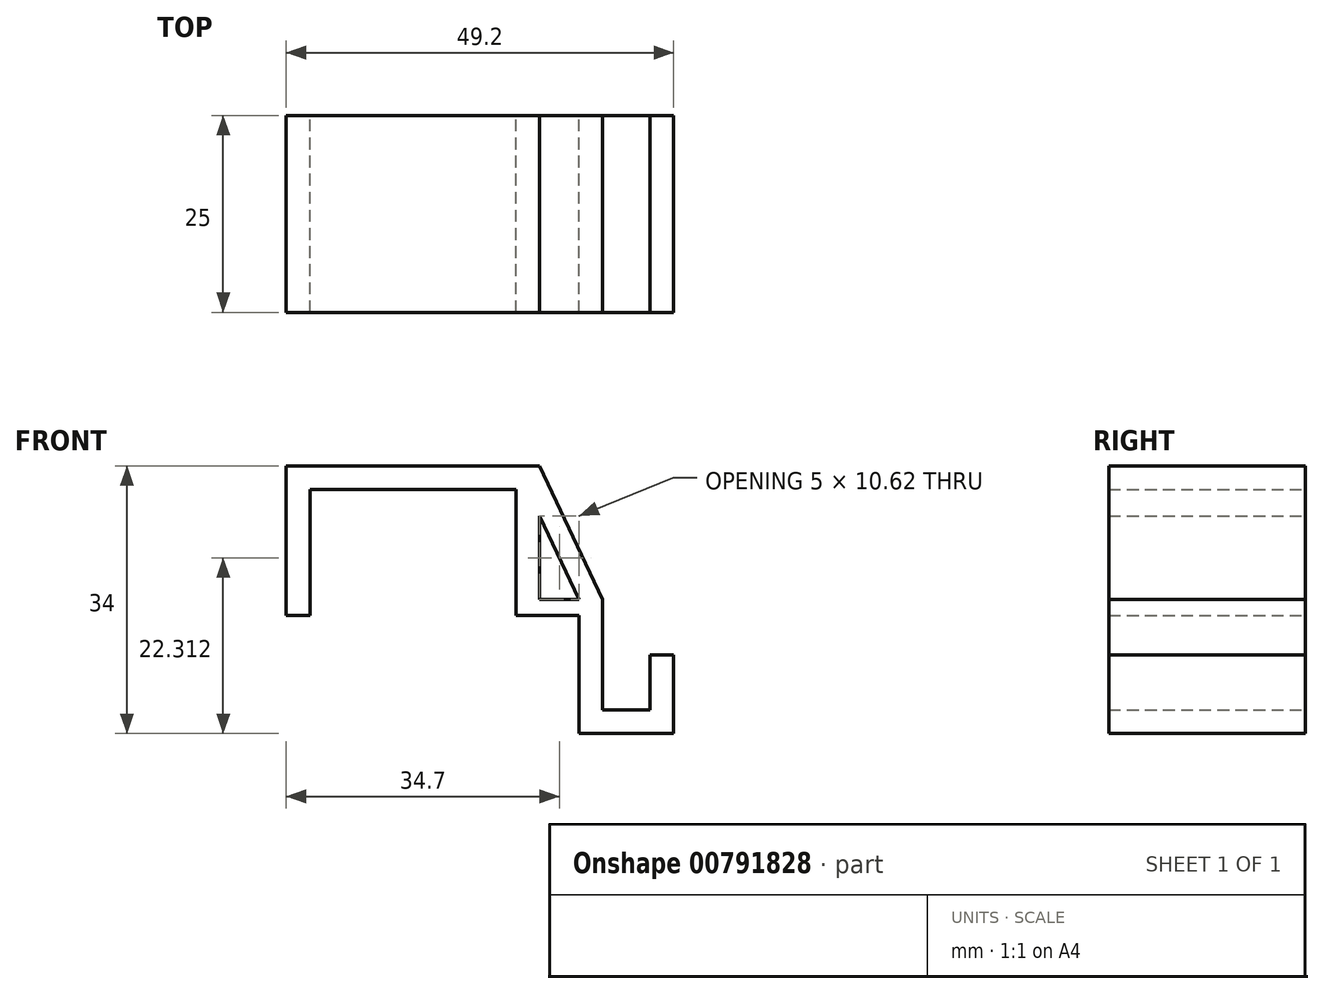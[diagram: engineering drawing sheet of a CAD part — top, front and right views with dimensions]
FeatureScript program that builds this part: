
annotation { "Feature Type Name" : "Feature", "Feature Type Description" : "" }
export const myFeature = defineFeature(function(context is Context, id is Id, definition is map)
    precondition{}
    {
        {
            var Q0;
            Q0=qCreatedBy(makeId("Front.planeOp"),FACE);
            var sketch = newSketch(context, id + "F0", { "sketchPlane" : qUnion([Q0])});
            skLineSegment(sketch, "E0.bottom", {"start": v(-13.1, -8) * mm, "end": v(13.1, -8) * mm});
            skLineSegment(sketch, "E0.top", {"start": v(-13.1, 8) * mm, "end": v(13.1, 8) * mm});
            skLineSegment(sketch, "E0.left", {"start": v(-13.1, -8) * mm, "end": v(-13.1, 8) * mm});
            skLineSegment(sketch, "E0.right", {"start": v(13.1, -8) * mm, "end": v(13.1, 8) * mm});
            skPoint(sketch, "E0.middle", {"position": v(0, 0) * mm});
            skLineSegment(sketch, "E1.bottom", {"start": v(13.1, 8) * mm, "end": v(16.1, 8) * mm, "construction": true});
            skLineSegment(sketch, "E1.top", {"start": v(13.1, 11) * mm, "end": v(16.1, 11) * mm, "construction": true});
            skLineSegment(sketch, "E1.left", {"start": v(13.1, 8) * mm, "end": v(13.1, 11) * mm, "construction": true});
            skLineSegment(sketch, "E1.right", {"start": v(16.1, 8) * mm, "end": v(16.1, 11) * mm, "construction": true});
            skLineSegment(sketch, "E2.bottom", {"start": v(-13.1, 8) * mm, "end": v(-16.1, 8) * mm, "construction": true});
            skLineSegment(sketch, "E2.top", {"start": v(-13.1, 11) * mm, "end": v(-16.1, 11) * mm, "construction": true});
            skLineSegment(sketch, "E2.left", {"start": v(-13.1, 8) * mm, "end": v(-13.1, 11) * mm, "construction": true});
            skLineSegment(sketch, "E2.right", {"start": v(-16.1, 8) * mm, "end": v(-16.1, 11) * mm, "construction": true});
            skLineSegment(sketch, "E3.bottom", {"start": v(-16.1, 11) * mm, "end": v(-13.1, 11) * mm});
            skLineSegment(sketch, "E3.top", {"start": v(-16.1, -8) * mm, "end": v(-13.1, -8) * mm});
            skLineSegment(sketch, "E3.left", {"start": v(-16.1, 11) * mm, "end": v(-16.1, -8) * mm});
            skLineSegment(sketch, "E3.right", {"start": v(-13.1, 11) * mm, "end": v(-13.1, -8) * mm});
            skLineSegment(sketch, "E4.bottom", {"start": v(-16.1, 11) * mm, "end": v(16.1, 11) * mm});
            skLineSegment(sketch, "E4.top", {"start": v(-16.1, 8) * mm, "end": v(16.1, 8) * mm});
            skLineSegment(sketch, "E4.left", {"start": v(-16.1, 11) * mm, "end": v(-16.1, 8) * mm});
            skLineSegment(sketch, "E4.right", {"start": v(16.1, 11) * mm, "end": v(16.1, 8) * mm});
            skLineSegment(sketch, "E5.bottom", {"start": v(16.1, 11) * mm, "end": v(13.1, 11) * mm});
            skLineSegment(sketch, "E5.top", {"start": v(16.1, -8) * mm, "end": v(13.1, -8) * mm});
            skLineSegment(sketch, "E5.left", {"start": v(16.1, 11) * mm, "end": v(16.1, -8) * mm});
            skLineSegment(sketch, "E5.right", {"start": v(13.1, 11) * mm, "end": v(13.1, -8) * mm});
            skLineSegment(sketch, "E6.bottom", {"start": v(16.1, -8) * mm, "end": v(24.1, -8) * mm});
            skLineSegment(sketch, "E6.top", {"start": v(16.1, -6) * mm, "end": v(24.1, -6) * mm});
            skLineSegment(sketch, "E6.left", {"start": v(16.1, -8) * mm, "end": v(16.1, -6) * mm});
            skLineSegment(sketch, "E6.right", {"start": v(24.1, -8) * mm, "end": v(24.1, -6) * mm});
            skLineSegment(sketch, "E7.bottom", {"start": v(24.1, -8) * mm, "end": v(21.1, -8) * mm});
            skLineSegment(sketch, "E7.top", {"start": v(24.1, -23) * mm, "end": v(21.1, -23) * mm});
            skLineSegment(sketch, "E7.left", {"start": v(24.1, -8) * mm, "end": v(24.1, -23) * mm});
            skLineSegment(sketch, "E7.right", {"start": v(21.1, -8) * mm, "end": v(21.1, -23) * mm});
            skLineSegment(sketch, "E8.bottom", {"start": v(24.1, -23) * mm, "end": v(33.1, -23) * mm});
            skLineSegment(sketch, "E8.top", {"start": v(24.1, -20) * mm, "end": v(33.1, -20) * mm});
            skLineSegment(sketch, "E8.left", {"start": v(24.1, -23) * mm, "end": v(24.1, -20) * mm});
            skLineSegment(sketch, "E8.right", {"start": v(33.1, -23) * mm, "end": v(33.1, -20) * mm});
            skLineSegment(sketch, "E9.bottom", {"start": v(33.1, -20) * mm, "end": v(30.1, -20) * mm});
            skLineSegment(sketch, "E9.top", {"start": v(33.1, -13) * mm, "end": v(30.1, -13) * mm});
            skLineSegment(sketch, "E9.left", {"start": v(33.1, -20) * mm, "end": v(33.1, -13) * mm});
            skLineSegment(sketch, "E9.right", {"start": v(30.1, -20) * mm, "end": v(30.1, -13) * mm});
            skLineSegment(sketch, "E10", {"start": v(16.1, 11) * mm, "end": v(24.1, -6) * mm});
            skLineSegment(sketch, "E11", {"start": v(21.1, -6) * mm, "end": v(16.1, 4.62) * mm});
            skSolve(sketch);
        }
        {
            var Q0;
            {var subQ0=sQuery(id+"F0.wireOp",EDGE,"E0.left");Q0=makeQuery(id+"F0.imprint","IMPRINT",FACE,{"disambiguationData":[TD([[makeQuery(id+"F0.imprint","IMPRINT",EDGE,{"derivedFrom":subQ0}),1.0]])]});}
            var Q1;
            {var subQ0=sQuery(id+"F0.wireOp",EDGE,"E3.bottom");Q1=makeQuery(id+"F0.imprint","IMPRINT",FACE,{"disambiguationData":[TD([[makeQuery(id+"F0.imprint","IMPRINT",EDGE,{"derivedFrom":subQ0}),-1.0]])]});}
            var Q2;
            Q2=makeQuery(id+"F0.imprint","IMPRINT",FACE,{"disambiguationData":[TD([[makeQuery(id+"F0.imprint","IMPRINT",EDGE,{"derivedFrom":sQuery(id+"F0.wireOp",EDGE,"E0.top")}),1.0]])]});
            var Q3;
            {var subQ0=sQuery(id+"F0.wireOp",EDGE,"E4.right");Q3=makeQuery(id+"F0.imprint","IMPRINT",FACE,{"disambiguationData":[TD([[makeQuery(id+"F0.imprint","IMPRINT",EDGE,{"derivedFrom":subQ0}),-1.0]])]});}
            var Q4;
            {var subQ4=sQuery(id+"F0.wireOp",EDGE,"E0.right");Q4=makeQuery(id+"F0.imprint","IMPRINT",FACE,{"disambiguationData":[TD([[makeQuery(id+"F0.imprint","IMPRINT",EDGE,{"derivedFrom":subQ4}),-1.0]])]});}
            var Q5;
            {var subQ1=sQuery(id+"F0.wireOp",EDGE,"E4.right");Q5=makeQuery(id+"F0.imprint","IMPRINT",FACE,{"disambiguationData":[TD([[makeQuery(id+"F0.imprint","IMPRINT",EDGE,{"derivedFrom":subQ1}),1.0]])]});}
            var Q6;
            {var subQ4=sQuery(id+"F0.wireOp",EDGE,"E6.right");Q6=makeQuery(id+"F0.imprint","IMPRINT",FACE,{"disambiguationData":[TD([[makeQuery(id+"F0.imprint","IMPRINT",EDGE,{"derivedFrom":subQ4}),1.0]])]});}
            var Q7;
            {var subQ1=sQuery(id+"F0.wireOp",EDGE,"E7.top");Q7=makeQuery(id+"F0.imprint","IMPRINT",FACE,{"disambiguationData":[TD([[makeQuery(id+"F0.imprint","IMPRINT",EDGE,{"derivedFrom":subQ1}),-1.0]])]});}
            var Q8;
            {var subQ5=sQuery(id+"F0.wireOp",EDGE,"E8.bottom");Q8=makeQuery(id+"F0.imprint","IMPRINT",FACE,{"disambiguationData":[TD([[makeQuery(id+"F0.imprint","IMPRINT",EDGE,{"derivedFrom":subQ5}),1.0]])]});}
            var Q9;
            Q9=makeQuery(id+"F0.imprint","IMPRINT",FACE,{"disambiguationData":[TD([[makeQuery(id+"F0.imprint","IMPRINT",EDGE,{"derivedFrom":sQuery(id+"F0.wireOp",EDGE,"E9.top")}),1.0]])]});
            extrude(context, id + "F1", {"entities" : qUnion([Q0, Q1, Q2, Q3, Q4, Q5, Q6, Q7, Q8, Q9]), "depth" : 25 * mm, "offsetDistance" : 25 * mm});
        }
    });
